# Revit family: QF_MACOM_BFT-70xxx
name_source: partatom
category: Equipamento especial
units: mm (PartAtom-declared; Revit-internal decimal feet)

## family parameters
Com base no plano de trabalho = Não
Compartilhado = Não
Corte com vazios quando carregada = Não
Cota do conector redondo = Utilizar diâmetro
Número OmniClass = 23.40.40.14.24.14
Ponto de cálculo do ambiente = Não
Sempre na vertical = Sim
Tipo de parte = Normal
Título OmniClass = Service Line Equipment

## types (5) — shared parameters
Fabricante = MACOM
URL = https://www.acosmacom.com.br
zero-valued in all types: Elevação padrão

## per-type parameters (varying)
| type | Center Feet | Descrição | Door 2 Posicion | Door 3 | Door 3 Posicion | Door 4 | Door 4 Posicion | Door 5 | Door QTY | Door Width | Length Actual |
| BFT-70250 | Sim | BUFFET FECHADO INOX MACOM ESP. TRASEIRO - 2500X700X900mm    
BUFFET FECHADO INOX MACOM ESP. TRASEIRO - 2500X700X900mm | 936  [stored 3.07087 ft] | Sim | 976  [stored 3.2021 ft] | Sim | 1912  [stored 6.27297 ft] | Sim | 5 | 468  [stored 1.53543 ft] | 2500  [stored 8.2021 ft] |
| BFT-70200 | Não | BUFFET FECHADO INOX MACOM ESP. TRASEIRO - 2000X700X900mm  
BUFFET FECHADO INOX MACOM ESP. TRASEIRO - 700X700X900mm | 940  [stored 3.08399 ft] | Sim | 980  [stored 3.21522 ft] | Sim | 1920  [stored 6.29921 ft] | Não | 4 | 470  [stored 1.54199 ft] | 2000  [stored 6.56168 ft] |
| BFT-70180 | Não | BUFFET FECHADO INOX MACOM ESP. TRASEIRO - 1800X700X900mm | 840  [stored 2.75591 ft] | Sim | 880  [stored 2.88714 ft] | Sim | 1720 | Não | 4 | 420  [stored 1.37795 ft] | 1800  [stored 5.90551 ft] |
| BFT-70140 | Não | BUFFET FECHADO INOX MACOM ESP. TRASEIRO - 1400X700X900mm  
BUFFET FECHADO INOX MACOM ESP. TRASEIRO - 700X700X900mm | 853 | Sim | 893 | Não | 427 | Não | 3 | 427 | 1400  [stored 4.59318 ft] |
| BFT-7070 | Não | BUFFET FECHADO INOX MACOM ESP. TRASEIRO - 700X700X900mm   
BUFFET FECHADO INOX MACOM ESP. TRASEIRO - 700X700X900mm | 620  [stored 2.03412 ft] | Não | 0  [stored 0 ft] | Não | 310  [stored 1.01706 ft] | Não | 2 | 310  [stored 1.01706 ft] | 700  [stored 2.29659 ft] |

note: column(s) folded — value = type name in every type: Modelo

note: [stored X ft] marks values corroborated as IEEE doubles in the binary element streams (Revit-internal decimal feet)
